# Revit family: Safety & Protection_Barrier_UltiGroup_Pedestrian Guard Rail
name_source: partatom
category: Generic Models
revit_build: Autodesk Revit Architecture 2016 (Build: 20150220_1215(x64)
units: mm (PartAtom-declared; Revit-internal decimal feet)

## family parameters
Always vertical = Yes
Can host rebar = No
Cut with Voids When Loaded = No
OmniClass Number = 23.40.10.14.27
OmniClass Title = Bollards
Part Type = Normal
Room Calculation Point = No
Round Connector Dimension = Use Diameter
Shared = No
Work Plane-Based = No

## types (2) — shared parameters
Description = Impactable PVC Pedestrian Guard Rail
Fax = 07 846 2467
Manufacturer = UltiGroup
PVC Black = PVC Black
PVC Post Insert = 10 mm  [stored 0.0328084 ft]
PVC Yellow = PVC Yellow
Plate Length 1 = 180 mm  [stored 0.590551 ft]
Plate Length 2 = 160 mm  [stored 0.524934 ft]
Post Distance = 1500 mm  [stored 4.92126 ft]
SS Bolts = Yes
Send Message = http://ultigroup.co.nz
Stainless Steel = SS Bolts
Steel Black = Steel Black
Steel Support Height = 300 mm
URL = www.ultigroup.co.nz
zero-valued in all types: InstallationGroup_ANZRS, ModifiedIssue_ANZRS

## per-type parameters (varying)
| type | PED 150 | PED 90 |
| PED 150 | Yes | No |
| PED 90 | No | Yes |

note: column(s) folded — value = type name in every type: Model

note: [stored X ft] marks values corroborated as IEEE doubles in the binary element streams (Revit-internal decimal feet)

## geometry (parser evidence)
native form markers: Sweep x3
no freeform markers — native parametric forms only
